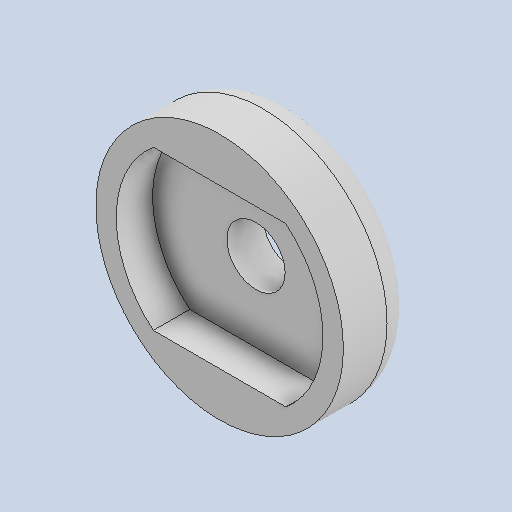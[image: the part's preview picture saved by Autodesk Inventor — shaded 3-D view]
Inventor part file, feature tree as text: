
AUTODESK INVENTOR PART (.ipt)
format: ipt  version: 2022 (Build 260153070, 153G)  size: 137,216 bytes
history: native  units: in
note: dims shown in document units (in); Inventor stores cm internally (conversion verified against a paired STEP export)
features: other x3, sketch x2
ambient origin geometry x8: Origin, YZ Plane, XZ Plane, XY Plane, X Axis, Y Axis, Z Axis, Center Point
bodies: Solid1 (feature_tree)
feature tree (5):
  other  "EncoderV2CAP.ipt"
  other  "Solid1::EncoderV2CAP.ipt"
  other  "TaggingFeature1"
  sketch  "Sketch1"  dims[d0=0.3937in]
  sketch  "Sketch4"
